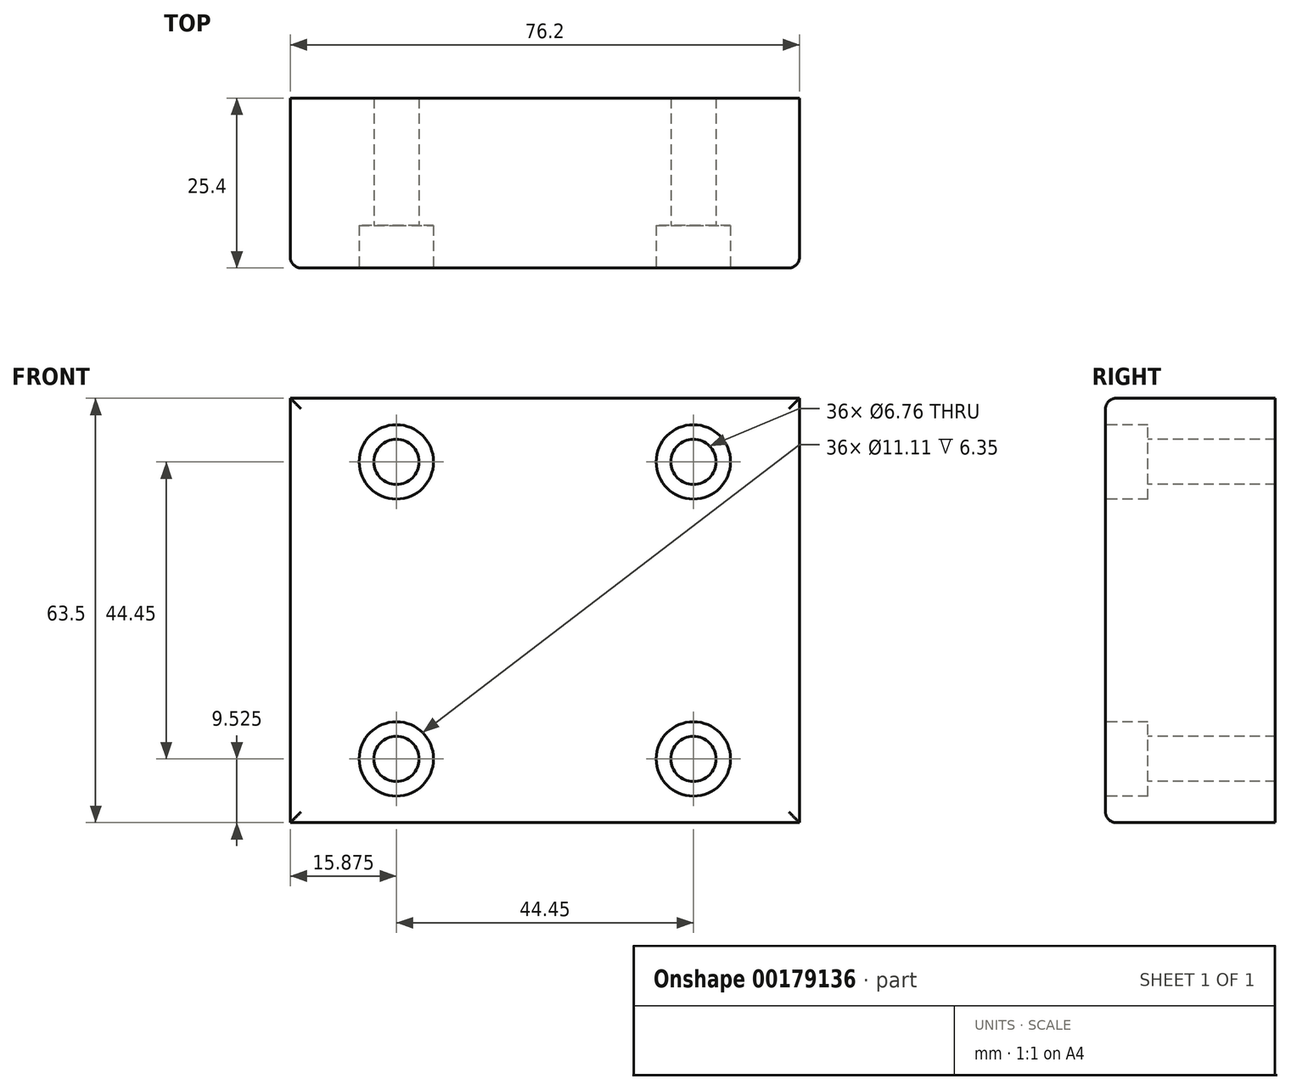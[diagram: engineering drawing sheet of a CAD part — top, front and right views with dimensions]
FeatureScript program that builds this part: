
annotation { "Feature Type Name" : "Feature", "Feature Type Description" : "" }
export const myFeature = defineFeature(function(context is Context, id is Id, definition is map)
    precondition{}
    {
        {
            var Q0;
            Q0=qCreatedBy(makeId("Front.planeOp"),FACE);
            var sketch = newSketch(context, id + "F0", { "sketchPlane" : qUnion([Q0])});
            skLineSegment(sketch, "E0.bottom", {"start": v(-38.1, 31.75) * mm, "end": v(38.1, 31.75) * mm});
            skLineSegment(sketch, "E0.top", {"start": v(-38.1, -31.75) * mm, "end": v(38.1, -31.75) * mm});
            skLineSegment(sketch, "E0.left", {"start": v(-38.1, 31.75) * mm, "end": v(-38.1, -31.75) * mm});
            skLineSegment(sketch, "E0.right", {"start": v(38.1, 31.75) * mm, "end": v(38.1, -31.75) * mm});
            skPoint(sketch, "E0.middle", {"position": v(0, 0) * mm});
            skSolve(sketch);
        }
        {
            var Q0;
            Q0=makeQuery(id+"F0.imprint","IMPRINT",FACE,{"disambiguationData":[TD([[makeQuery(id+"F0.imprint","IMPRINT",EDGE,{"derivedFrom":sQuery(id+"F0.wireOp",EDGE,"E0.bottom")}),-1.0]])]});
            extrude(context, id + "F1", {"entities" : qUnion([Q0]), "depth" : 25.4 * mm});
        }
        {
            var Q0;
            Q0=makeQuery(id+"F1.opExtrude","CAP_FACE",FACE,{"disambiguationData":[OSD([sQuery(id+"F0.wireOp",EDGE,"E0.bottom"),sQuery(id+"F0.wireOp",EDGE,"E0.top"),sQuery(id+"F0.wireOp",EDGE,"E0.left"),sQuery(id+"F0.wireOp",EDGE,"E0.right")])],"isStart":false});
            var sketch = newSketch(context, id + "F2", { "sketchPlane" : qUnion([Q0])});
            skLineSegment(sketch, "E1.bottom", {"start": v(-22.22, 22.23) * mm, "end": v(22.23, 22.23) * mm});
            skLineSegment(sketch, "E1.top", {"start": v(-22.23, -22.23) * mm, "end": v(22.22, -22.23) * mm});
            skLineSegment(sketch, "E1.left", {"start": v(-22.22, 22.23) * mm, "end": v(-22.23, -22.23) * mm});
            skLineSegment(sketch, "E1.right", {"start": v(22.23, 22.23) * mm, "end": v(22.22, -22.23) * mm});
            skPoint(sketch, "E1.middle", {"position": v(0, 0) * mm});
            skSolve(sketch);
        }
        {
            var Q0;
            Q0=sQuery(id+"F2.wireOp",VERTEX,"E1.left.start");
            var Q1;
            Q1=sQuery(id+"F2.wireOp",VERTEX,"E1.right.start");
            var Q2;
            Q2=sQuery(id+"F2.wireOp",VERTEX,"E1.top.end");
            var Q3;
            Q3=sQuery(id+"F2.wireOp",VERTEX,"E1.left.end");
            var Q4;
            Q4=makeQuery(id+"F1.opExtrude","SWEPT_BODY",BODY,{"disambiguationData":[OSD([sQuery(id+"F0.wireOp",EDGE,"E0.bottom"),sQuery(id+"F0.wireOp",EDGE,"E0.top"),sQuery(id+"F0.wireOp",EDGE,"E0.left"),sQuery(id+"F0.wireOp",EDGE,"E0.right")])]});
            hole(context, id + "F3", {"style" : HoleStyle.C_BORE, "endStyle" : HoleEndStyle.THROUGH, "standardTappedOrClearance" : lookupTablePath({ "standard" : "ANSI", "fit" : "Normal (ASME)", "size" : "1/4", "type" : "Clearance" }), "standardBlindInLast" : lookupTablePath({ "fit" : "Free", "standard" : "ANSI", "size" : "1/4", "type" : "Clearance" }), "holeDiameter" : 6.76 * mm, "cBoreDiameter" : 11.1 * mm, "cBoreDepth" : 6.35 * mm, "locations" : qUnion([Q0, Q1, Q2, Q3]), "scope" : qUnion([Q4]), "isTappedThrough" : true});
        }
        {
            var Q0;
            Q0=makeQuery(id+"F1.opExtrude","CAP_EDGE",EDGE,{"disambiguationData":[OSD([sQuery(id+"F0.wireOp",EDGE,"E0.bottom")])],"isStart":false});
            var Q1;
            Q1=makeQuery(id+"F1.opExtrude","CAP_EDGE",EDGE,{"disambiguationData":[OSD([sQuery(id+"F0.wireOp",EDGE,"E0.right")])],"isStart":false});
            var Q2;
            Q2=makeQuery(id+"F1.opExtrude","CAP_EDGE",EDGE,{"disambiguationData":[OSD([sQuery(id+"F0.wireOp",EDGE,"E0.top")])],"isStart":false});
            var Q3;
            Q3=makeQuery(id+"F1.opExtrude","CAP_EDGE",EDGE,{"disambiguationData":[OSD([sQuery(id+"F0.wireOp",EDGE,"E0.left")])],"isStart":false});
            fillet(context, id + "F4", {"entities" : qUnion([Q0, Q1, Q2, Q3]), "radius" : 1.59 * mm, "allowEdgeOverflow" : false});
        }
    });
